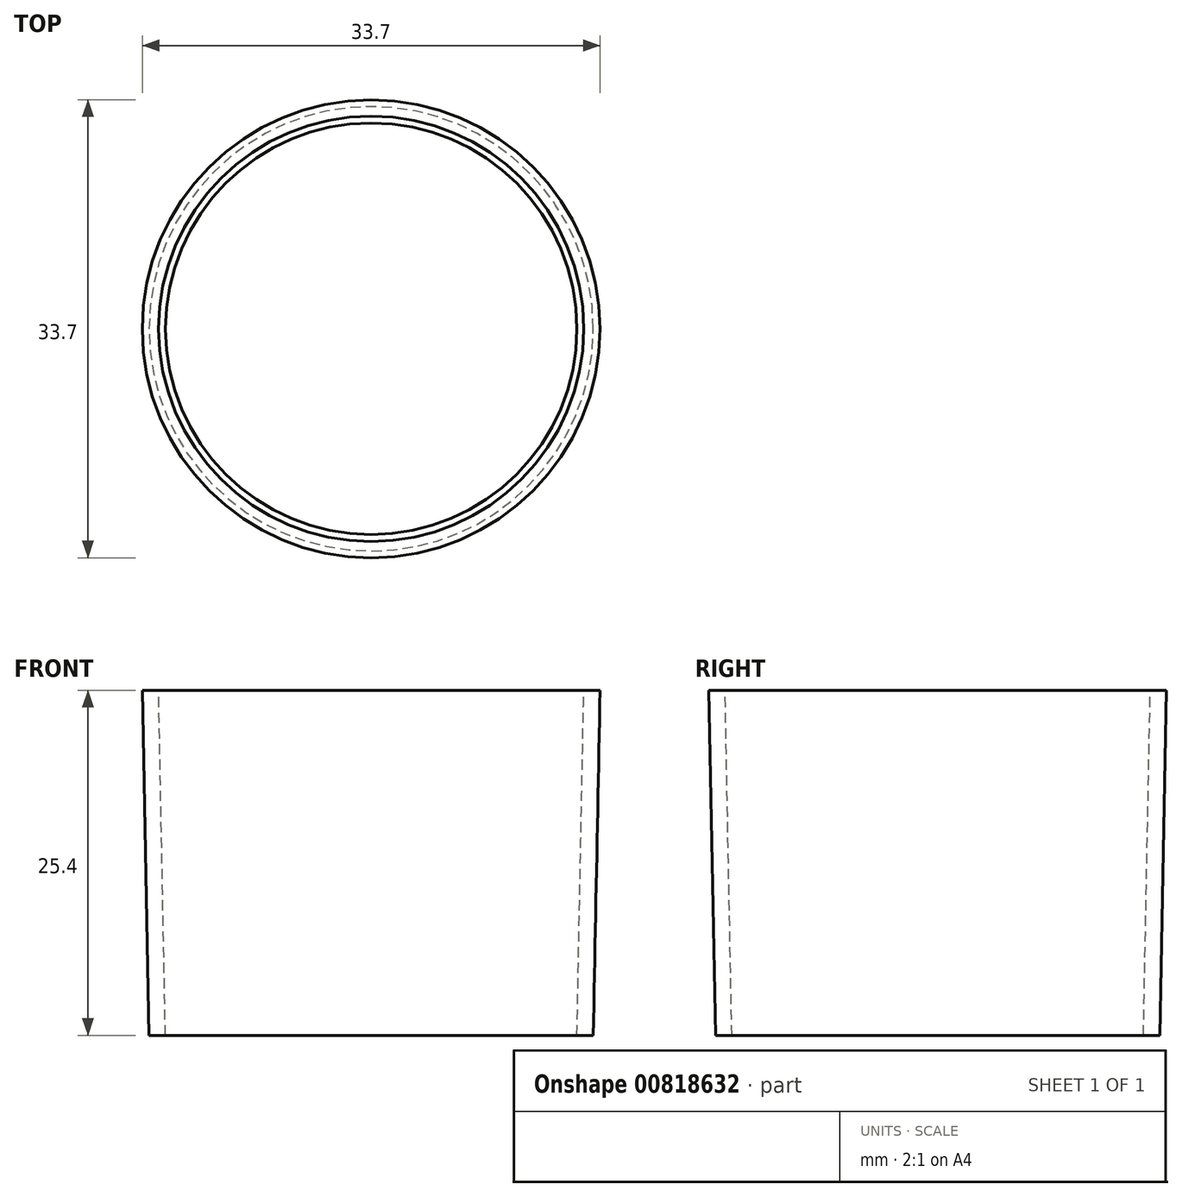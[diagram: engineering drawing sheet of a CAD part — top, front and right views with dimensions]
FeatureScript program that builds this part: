
annotation { "Feature Type Name" : "Feature", "Feature Type Description" : "" }
export const myFeature = defineFeature(function(context is Context, id is Id, definition is map)
    precondition{}
    {
        {
            var Q0;
            Q0=qCreatedBy(makeId("Top.planeOp"),FACE);
            cPlane(context, id + "F0", {"entities" : qUnion([Q0]), "cplaneType" : CPlaneType.OFFSET, "offset" : 25.4 * mm, "width" : 150 * mm, "height" : 150 * mm});
        }
        {
            var Q0;
            Q0=qCreatedBy(id+"F0.planeOp",FACE);
            var sketch = newSketch(context, id + "F1", { "sketchPlane" : qUnion([Q0])});
            skCircle(sketch, "E0", {"center": v(0, 0) * mm, "radius": 16.85 * mm});
            skSolve(sketch);
        }
        {
            var Q0;
            Q0=qCreatedBy(makeId("Top.planeOp"),FACE);
            var sketch = newSketch(context, id + "F2", { "sketchPlane" : qUnion([Q0])});
            skCircle(sketch, "E1", {"center": v(0, 0) * mm, "radius": 16.35 * mm});
            skSolve(sketch);
        }
        {
            var Q0;
            Q0 = qSketchRegion(id + "F2", true);
            var Q1;
            Q1 = qSketchRegion(id + "F1", true);
            loft(context, id + "F3", {"sheetProfilesArray" : [{ "sheetProfileEntities" : qUnion([Q0]) }, { "sheetProfileEntities" : qUnion([Q1]) }]});
        }
        {
            var Q0;
            Q0=qCreatedBy(makeId("Top.planeOp"),FACE);
            var sketch = newSketch(context, id + "F4", { "sketchPlane" : qUnion([Q0])});
            skCircle(sketch, "E2", {"center": v(0, 0) * mm, "radius": 15.15 * mm});
            skSolve(sketch);
        }
        {
            var Q0;
            Q0=qCreatedBy(id+"F0.planeOp",FACE);
            var sketch = newSketch(context, id + "F5", { "sketchPlane" : qUnion([Q0])});
            skCircle(sketch, "E3", {"center": v(0, 0) * mm, "radius": 15.65 * mm});
            skSolve(sketch);
        }
        {
            var Q1;
            Q1 = qSketchRegion(id + "F4", true);
            var Q2;
            Q2 = qSketchRegion(id + "F5", true);
            loft(context, id + "F6", {"operationType" : NewBodyOperationType.REMOVE, "sheetProfilesArray" : [{ "sheetProfileEntities" : qUnion([Q1]) }, { "sheetProfileEntities" : qUnion([Q2]) }]});
        }
    });
